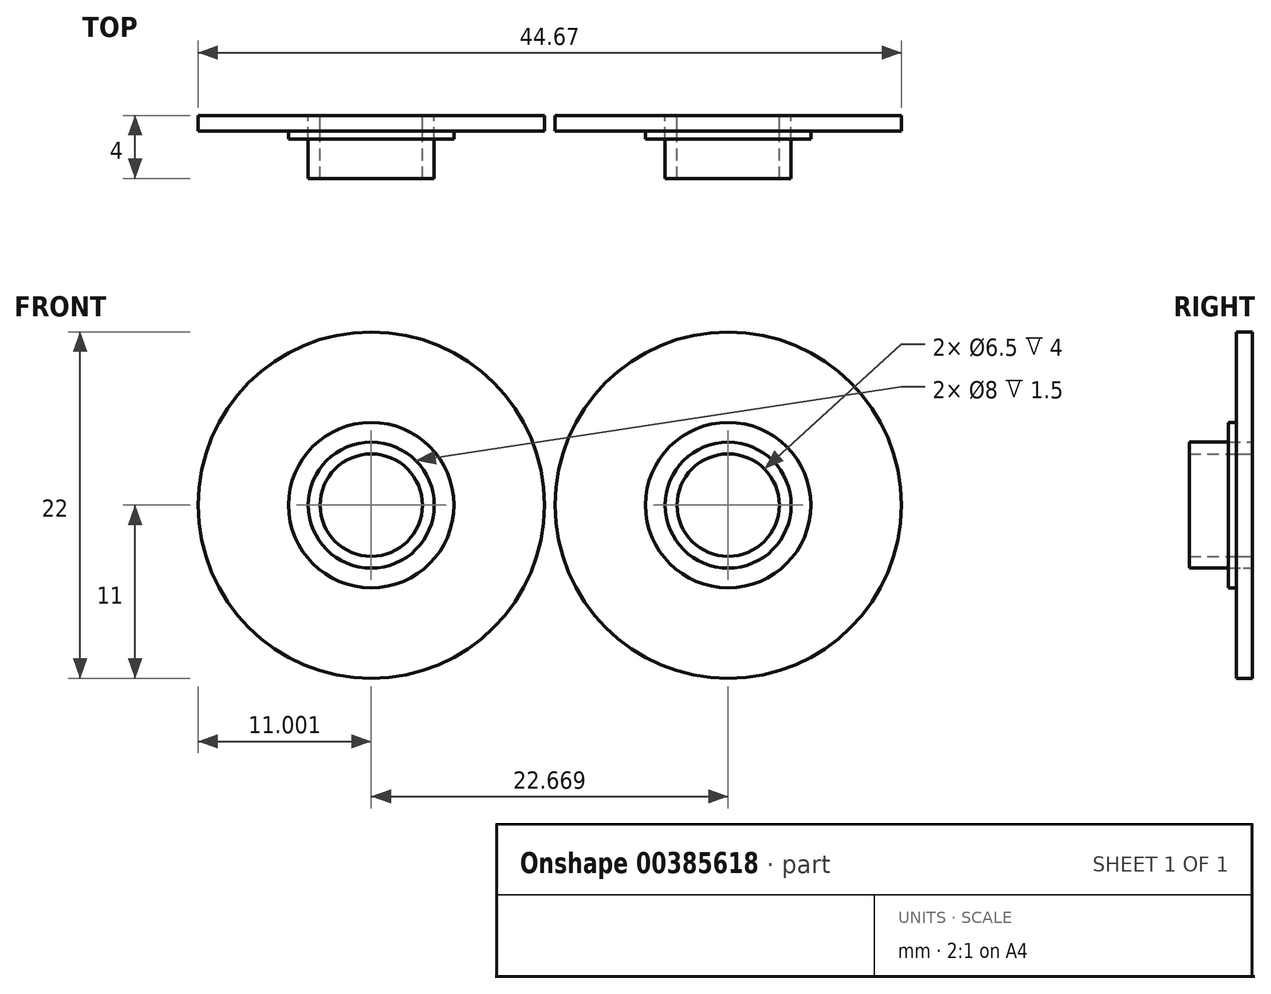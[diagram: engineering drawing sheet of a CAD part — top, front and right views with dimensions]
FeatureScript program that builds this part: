
annotation { "Feature Type Name" : "Feature", "Feature Type Description" : "" }
export const myFeature = defineFeature(function(context is Context, id is Id, definition is map)
    precondition{}
    {
        {
            var Q0;
            Q0=qCreatedBy(makeId("Front.planeOp"),FACE);
            var sketch = newSketch(context, id + "F0", { "sketchPlane" : qUnion([Q0])});
            skCircle(sketch, "E0", {"center": v(0, 0) * mm, "radius": 11 * mm});
            skCircle(sketch, "E1", {"center": v(0, 0) * mm, "radius": 5.25 * mm});
            skCircle(sketch, "E2", {"center": v(0, 0) * mm, "radius": 4 * mm});
            skCircle(sketch, "E3", {"center": v(0, 0) * mm, "radius": 3.25 * mm});
            skCircle(sketch, "E4", {"center": v(-22.67, 0) * mm, "radius": 11 * mm});
            skCircle(sketch, "E5", {"center": v(-22.67, 0) * mm, "radius": 5.25 * mm});
            skCircle(sketch, "E6", {"center": v(-22.67, 0) * mm, "radius": 4 * mm});
            skCircle(sketch, "E7", {"center": v(-22.67, 0) * mm, "radius": 3.25 * mm});
            skSolve(sketch);
        }
        {
            var Q0;
            Q0=makeQuery(id+"F0.imprint","IMPRINT",FACE,{"disambiguationData":[TD([[makeQuery(id+"F0.imprint","IMPRINT",EDGE,{"derivedFrom":sQuery(id+"F0.wireOp",EDGE,"E0")}),1.0]])]});
            var Q1;
            Q1=makeQuery(id+"F0.imprint","IMPRINT",FACE,{"disambiguationData":[TD([[makeQuery(id+"F0.imprint","IMPRINT",EDGE,{"derivedFrom":sQuery(id+"F0.wireOp",EDGE,"E3")}),1.0]])]});
            var Q2;
            Q2=makeQuery(id+"F0.imprint","IMPRINT",FACE,{"disambiguationData":[TD([[makeQuery(id+"F0.imprint","IMPRINT",EDGE,{"derivedFrom":sQuery(id+"F0.wireOp",EDGE,"E4")}),1.0]])]});
            var Q3;
            Q3=makeQuery(id+"F0.imprint","IMPRINT",FACE,{"disambiguationData":[TD([[makeQuery(id+"F0.imprint","IMPRINT",EDGE,{"derivedFrom":sQuery(id+"F0.wireOp",EDGE,"E7")}),1.0]])]});
            extrude(context, id + "F1", {"entities" : qUnion([Q0, Q1, Q2, Q3]), "depth" : 1 * mm, "offsetDistance" : 25 * mm});
        }
        {
            var Q0;
            Q0=makeQuery(id+"F0.imprint","IMPRINT",FACE,{"disambiguationData":[TD([[makeQuery(id+"F0.imprint","IMPRINT",EDGE,{"derivedFrom":sQuery(id+"F0.wireOp",EDGE,"E1")}),1.0]])]});
            var Q1;
            Q1=makeQuery(id+"F0.imprint","IMPRINT",FACE,{"disambiguationData":[TD([[makeQuery(id+"F0.imprint","IMPRINT",EDGE,{"derivedFrom":sQuery(id+"F0.wireOp",EDGE,"E5")}),1.0]])]});
            extrude(context, id + "F2", {"entities" : qUnion([Q0, Q1]), "operationType" : NewBodyOperationType.ADD, "depth" : 1.5 * mm, "offsetDistance" : 25 * mm});
        }
        {
            var Q0;
            Q0=makeQuery(id+"F0.imprint","IMPRINT",FACE,{"disambiguationData":[TD([[makeQuery(id+"F0.imprint","IMPRINT",EDGE,{"derivedFrom":sQuery(id+"F0.wireOp",EDGE,"E2")}),1.0]])]});
            var Q1;
            Q1=makeQuery(id+"F0.imprint","IMPRINT",FACE,{"disambiguationData":[TD([[makeQuery(id+"F0.imprint","IMPRINT",EDGE,{"derivedFrom":sQuery(id+"F0.wireOp",EDGE,"E6")}),1.0]])]});
            extrude(context, id + "F3", {"entities" : qUnion([Q0, Q1]), "depth" : 4 * mm, "offsetDistance" : 25 * mm});
        }
    });
